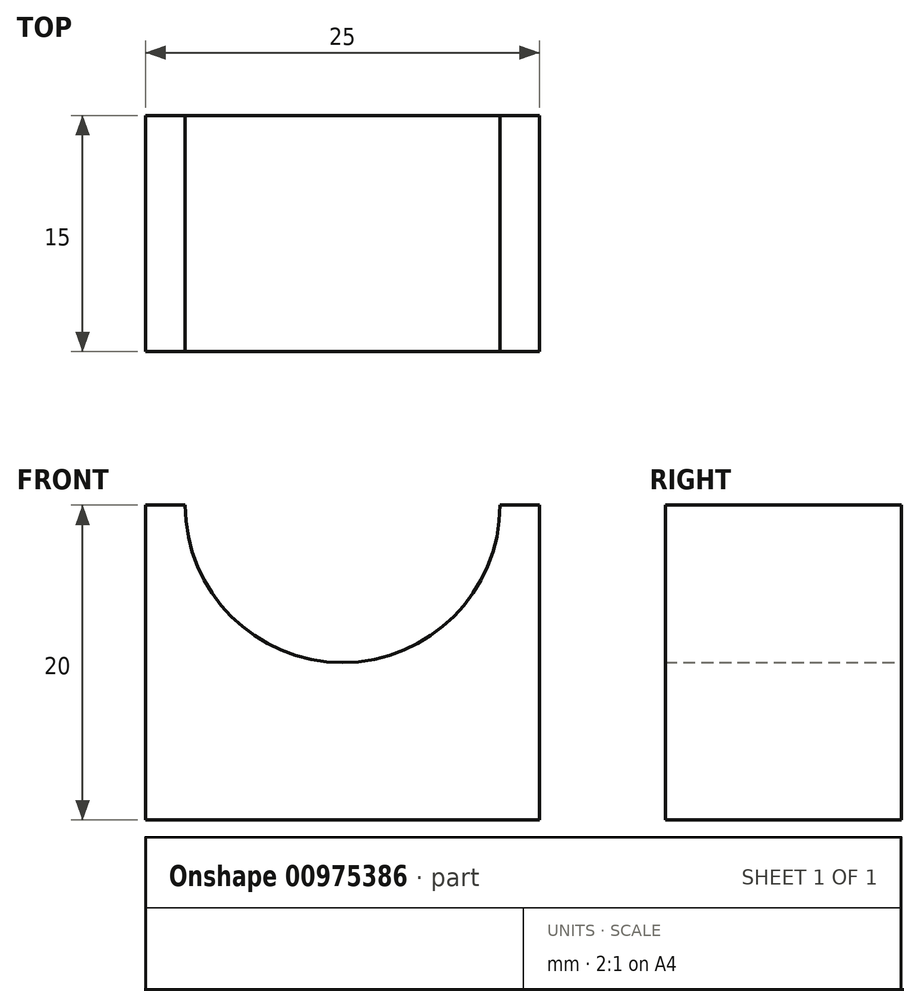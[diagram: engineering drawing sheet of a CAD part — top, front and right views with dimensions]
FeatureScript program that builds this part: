
annotation { "Feature Type Name" : "Feature", "Feature Type Description" : "" }
export const myFeature = defineFeature(function(context is Context, id is Id, definition is map)
    precondition{}
    {
        {
            var Q0;
            Q0=qCreatedBy(makeId("Front.planeOp"),FACE);
            var sketch = newSketch(context, id + "F0", { "sketchPlane" : qUnion([Q0])});
            skLineSegment(sketch, "E0.bottom", {"start": v(-1.4, 11.4) * mm, "end": v(23.6, 11.4) * mm});
            skLineSegment(sketch, "E0.top", {"start": v(-1.4, -8.6) * mm, "end": v(23.6, -8.6) * mm});
            skLineSegment(sketch, "E0.left", {"start": v(-1.4, 11.4) * mm, "end": v(-1.4, -8.6) * mm});
            skLineSegment(sketch, "E0.right", {"start": v(23.6, 11.4) * mm, "end": v(23.6, -8.6) * mm});
            skLineSegment(sketch, "E1", {"start": v(11.1, 11.4) * mm, "end": v(11.1, 1.4) * mm});
            skPoint(sketch, "E1.endSnap0", {"position": v(-1.4, 1.4) * mm});
            skLineSegment(sketch, "E2", {"start": v(11.1, 1.4) * mm, "end": v(11.1, 6.4) * mm});
            skLineSegment(sketch, "E3", {"start": v(11.1, 11.4) * mm, "end": v(11.1, 8.9) * mm});
            skCircle(sketch, "E4", {"center": v(11.1, 11.4) * mm, "radius": 10 * mm});
            skSolve(sketch);
        }
        {
            var Q0;
            Q0=makeQuery(id+"F0.imprint","IMPRINT",FACE,{"disambiguationData":[TD([[makeQuery(id+"F0.imprint","IMPRINT",EDGE,{"derivedFrom":sQuery(id+"F0.wireOp",EDGE,"E0.top")}),1.0]])]});
            extrude(context, id + "F1", {"entities" : qUnion([Q0]), "depth" : 15 * mm, "offsetDistance" : 25 * mm});
        }
    });
